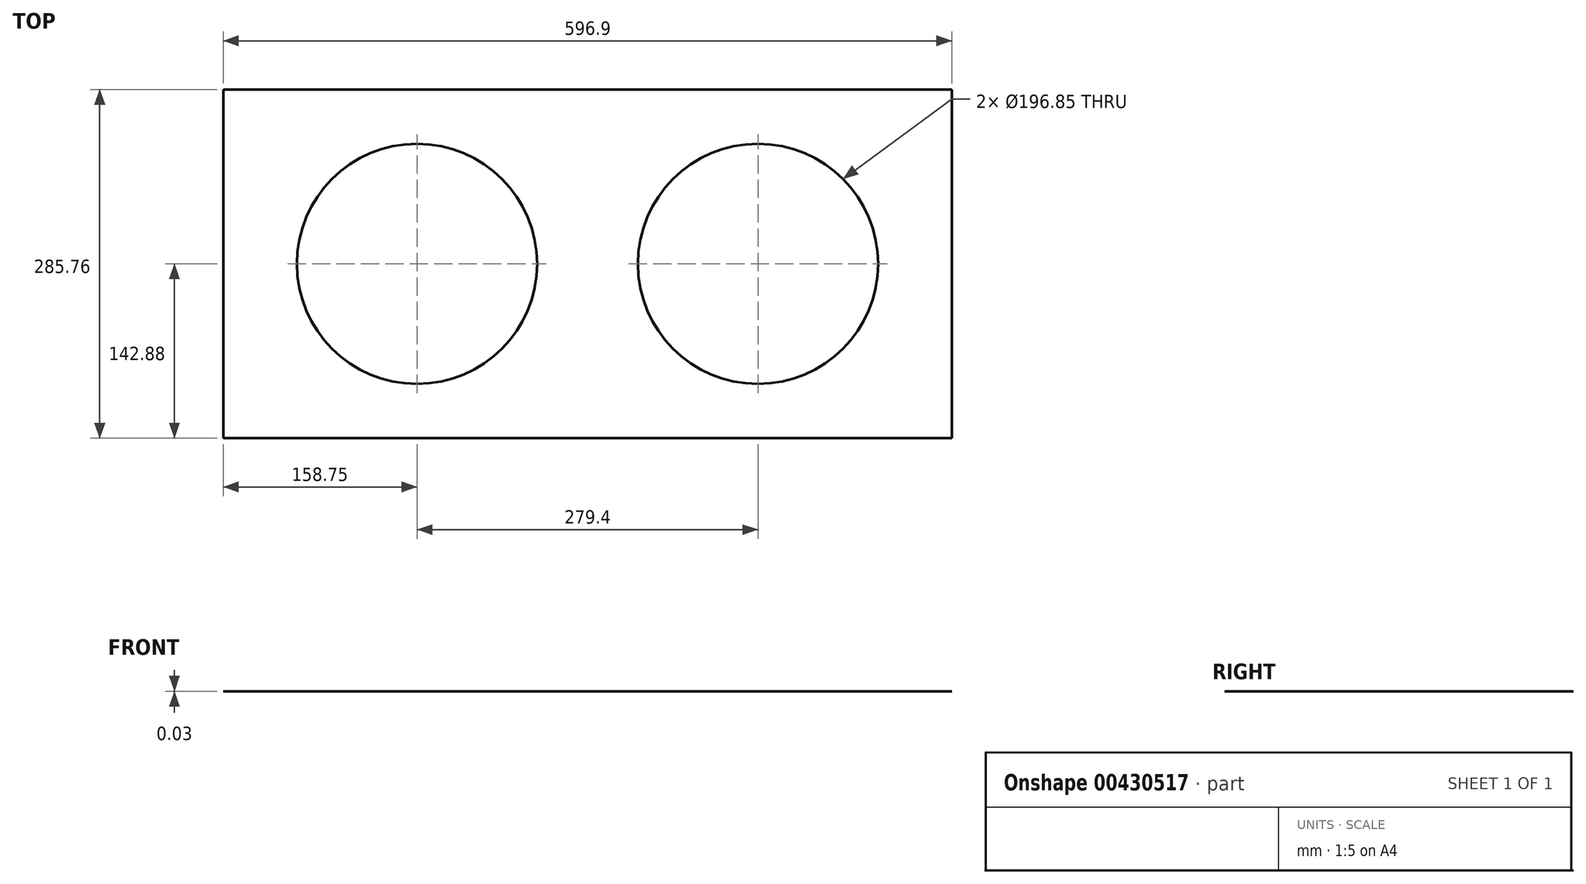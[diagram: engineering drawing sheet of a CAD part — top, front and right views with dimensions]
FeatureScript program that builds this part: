
annotation { "Feature Type Name" : "Feature", "Feature Type Description" : "" }
export const myFeature = defineFeature(function(context is Context, id is Id, definition is map)
    precondition{}
    {
        {
            var Q0;
            Q0=qCreatedBy(makeId("Top.planeOp"),FACE);
            var sketch = newSketch(context, id + "F0", { "sketchPlane" : qUnion([Q0])});
            skLineSegment(sketch, "E0.bottom", {"start": v(-298.45, 142.88) * mm, "end": v(298.45, 142.88) * mm});
            skLineSegment(sketch, "E0.top", {"start": v(-298.45, -142.87) * mm, "end": v(298.45, -142.87) * mm});
            skLineSegment(sketch, "E0.left", {"start": v(-298.45, 142.88) * mm, "end": v(-298.45, -142.87) * mm});
            skLineSegment(sketch, "E0.right", {"start": v(298.45, 142.88) * mm, "end": v(298.45, -142.87) * mm});
            skLineSegment(sketch, "E1", {"start": v(-298.45, 142.87) * mm, "end": v(298.45, -142.88) * mm, "construction": true});
            skCircle(sketch, "E2", {"center": v(-139.7, 0) * mm, "radius": 98.43 * mm});
            skCircle(sketch, "E3", {"center": v(139.7, 0) * mm, "radius": 98.43 * mm});
            skLineSegment(sketch, "E4", {"start": v(-139.7, 0) * mm, "end": v(139.7, 0) * mm, "construction": true});
            skSolve(sketch);
        }
        {
            var Q0;
            Q0=makeQuery(id+"F0.imprint","IMPRINT",FACE,{"disambiguationData":[TD([[makeQuery(id+"F0.imprint","IMPRINT",EDGE,{"derivedFrom":sQuery(id+"F0.wireOp",EDGE,"E0.bottom")}),-1.0]])]});
            extrude(context, id + "F1", {"entities" : qUnion([Q0]), "depth" : 13 / 406.4 * mm});
        }
    });
